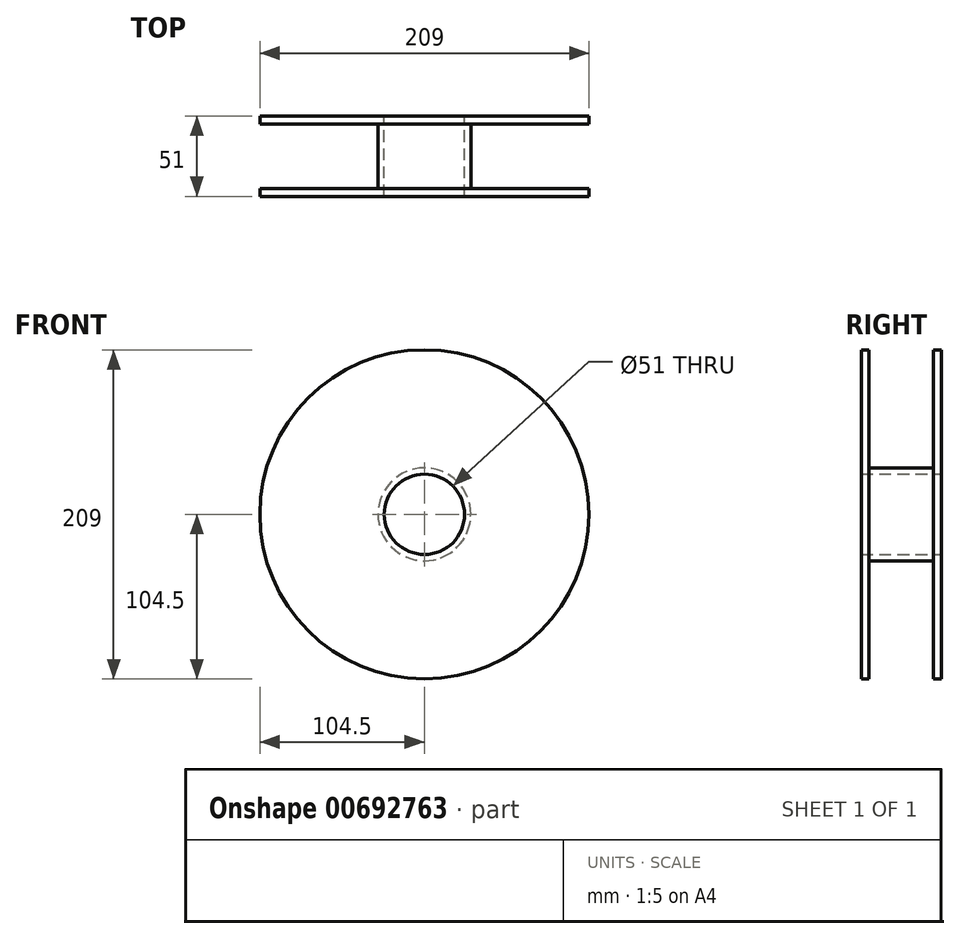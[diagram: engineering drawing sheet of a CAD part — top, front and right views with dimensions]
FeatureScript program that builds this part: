
annotation { "Feature Type Name" : "Feature", "Feature Type Description" : "" }
export const myFeature = defineFeature(function(context is Context, id is Id, definition is map)
    precondition{}
    {
        {
            var Q0;
            Q0=qCreatedBy(makeId("Front.planeOp"),FACE);
            var sketch = newSketch(context, id + "F0", { "sketchPlane" : qUnion([Q0])});
            skCircle(sketch, "E0", {"center": v(0, 0) * mm, "radius": 25.5 * mm});
            skCircle(sketch, "E1.0", {"center": v(0, 0) * mm, "radius": 29.5 * mm});
            skSolve(sketch);
        }
        {
            var Q0;
            Q0 = qSketchRegion(id + "F0", true);
            extrude(context, id + "F1", {"entities" : qUnion([Q0]), "depth" : 51 * mm, "offsetDistance" : 25 * mm, "symmetric" : true});
        }
        {
            var Q0;
            Q0=makeQuery(id+"F1.opExtrude","CAP_FACE",FACE,{"disambiguationData":[OSD([sQuery(id+"F0.wireOp",EDGE,"E0"),sQuery(id+"F0.wireOp",EDGE,"E1.0")])],"isStart":false});
            var sketch = newSketch(context, id + "F2", { "sketchPlane" : qUnion([Q0])});
            skCircle(sketch, "E2.0", {"center": v(0, 0) * mm, "radius": 29.5 * mm});
            skCircle(sketch, "E3.0", {"center": v(0, 0) * mm, "radius": 104.5 * mm});
            skSolve(sketch);
        }
        {
            var Q0;
            Q0 = qSketchRegion(id + "F2", true);
            extrude(context, id + "F3", {"entities" : qUnion([Q0]), "oppositeDirection" : true, "depth" : 5 * mm, "offsetDistance" : 25 * mm});
        }
        {
            var Q0;
            Q0=makeQuery(id+"F3.opExtrude","SWEPT_BODY",BODY,{"disambiguationData":[OSD([sQuery(id+"F2.wireOp",EDGE,"E2.0"),sQuery(id+"F2.wireOp",EDGE,"E3.0")])]});
            var Q1;
            Q1=qCreatedBy(makeId("Front.planeOp"),FACE);
            mirror(context, id + "F4", {"operationType" : NewBodyOperationType.ADD, "entities" : qUnion([Q0]), "mirrorPlane" : qUnion([Q1])});
        }
    });
